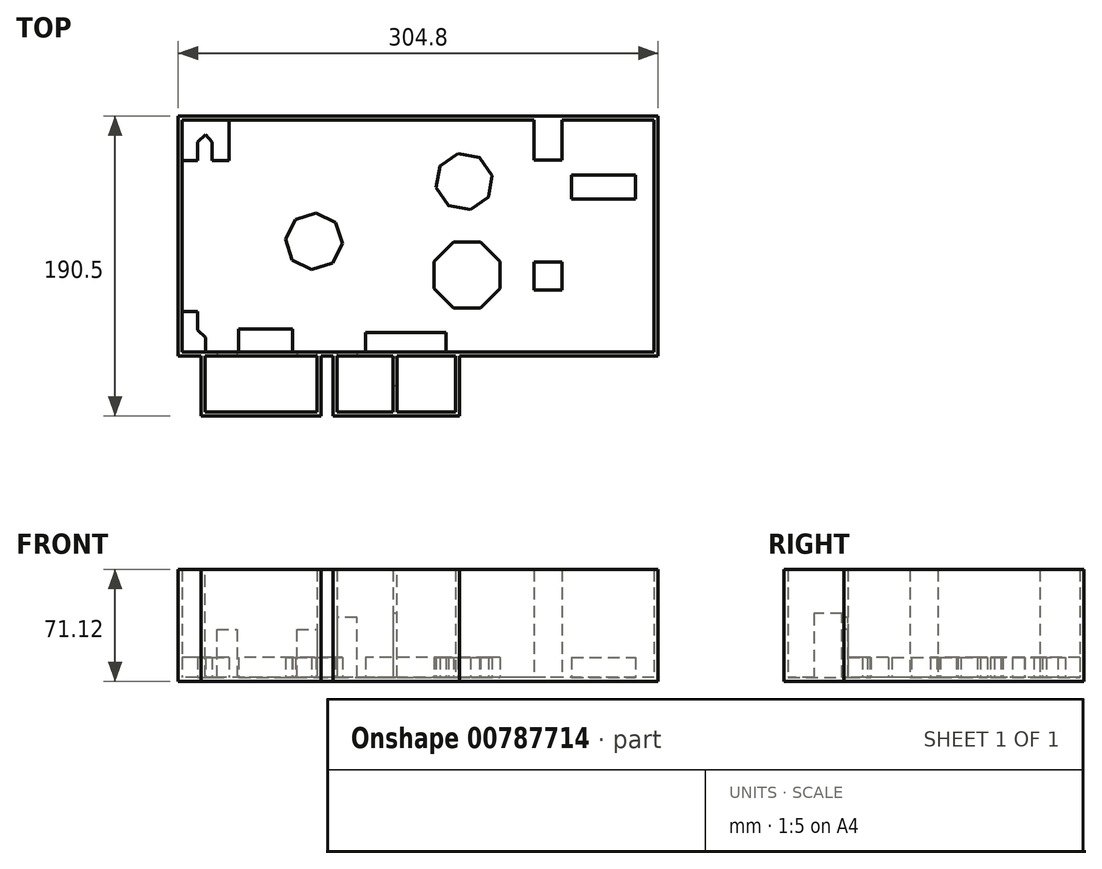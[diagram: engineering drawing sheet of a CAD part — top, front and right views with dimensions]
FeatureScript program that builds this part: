
annotation { "Feature Type Name" : "Feature", "Feature Type Description" : "" }
export const myFeature = defineFeature(function(context is Context, id is Id, definition is map)
    precondition{}
    {
        {
            var Q0;
            Q0=qCreatedBy(makeId("Top.planeOp"),FACE);
            var sketch = newSketch(context, id + "F0", { "sketchPlane" : qUnion([Q0])});
            skLineSegment(sketch, "E0.bottom", {"start": v(76.2, 76.2) * mm, "end": v(-228.6, 76.2) * mm});
            skLineSegment(sketch, "E0.top", {"start": v(76.2, -76.2) * mm, "end": v(-228.6, -76.2) * mm});
            skLineSegment(sketch, "E0.left", {"start": v(76.2, 76.2) * mm, "end": v(76.2, -76.2) * mm});
            skLineSegment(sketch, "E0.right", {"start": v(-228.6, 76.2) * mm, "end": v(-228.6, -76.2) * mm});
            skPoint(sketch, "E1", {"position": v(0, 76.2) * mm});
            skPoint(sketch, "E2", {"position": v(12.7, 76.2) * mm});
            skLineSegment(sketch, "E3", {"start": v(0, 76.2) * mm, "end": v(0, 50.8) * mm});
            skLineSegment(sketch, "E4", {"start": v(0, 50.8) * mm, "end": v(12.7, 50.8) * mm});
            skLineSegment(sketch, "E5", {"start": v(12.7, 50.8) * mm, "end": v(12.7, 76.2) * mm});
            skPoint(sketch, "E6", {"position": v(0, -31.67) * mm});
            skPoint(sketch, "E7", {"position": v(0, -18.97) * mm});
            skLineSegment(sketch, "E8", {"start": v(0, -31.67) * mm, "end": v(0, -18.97) * mm});
            skLineSegment(sketch, "E9", {"start": v(0, -18.97) * mm, "end": v(12.7, -18.97) * mm});
            skLineSegment(sketch, "E10", {"start": v(12.7, -18.97) * mm, "end": v(12.7, -31.67) * mm});
            skLineSegment(sketch, "E11", {"start": v(12.7, -31.67) * mm, "end": v(0, -31.67) * mm});
            skPoint(sketch, "E12", {"position": v(18.54, 76.2) * mm});
            skPoint(sketch, "E13", {"position": v(33.78, 76.2) * mm});
            skPoint(sketch, "E14", {"position": v(-228.6, -42.42) * mm});
            skPoint(sketch, "E15", {"position": v(-228.6, -17.02) * mm});
            skPoint(sketch, "E16", {"position": v(-201.42, -76.2) * mm});
            skPoint(sketch, "E17", {"position": v(-188.72, -76.2) * mm});
            skPoint(sketch, "E18", {"position": v(-150.62, -76.2) * mm});
            skPoint(sketch, "E19", {"position": v(-137.92, -76.2) * mm});
            skLineSegment(sketch, "E20", {"start": v(-201.42, -114.3) * mm, "end": v(-137.92, -114.3) * mm});
            skLineSegment(sketch, "E21", {"start": v(-137.92, -114.3) * mm, "end": v(-137.92, -76.2) * mm});
            skLineSegment(sketch, "E22", {"start": v(-201.42, -114.3) * mm, "end": v(-214.12, -114.3) * mm});
            skLineSegment(sketch, "E23", {"start": v(-214.12, -114.3) * mm, "end": v(-214.12, -76.2) * mm});
            skPoint(sketch, "E24", {"position": v(-130.3, -76.2) * mm});
            skLineSegment(sketch, "E25", {"start": v(-130.3, -76.2) * mm, "end": v(-130.3, -114.3) * mm});
            skLineSegment(sketch, "E26", {"start": v(-130.3, -114.3) * mm, "end": v(-92.2, -114.3) * mm});
            skLineSegment(sketch, "E27", {"start": v(-92.2, -114.3) * mm, "end": v(-49.89, -114.3) * mm});
            skLineSegment(sketch, "E28", {"start": v(-49.89, -114.3) * mm, "end": v(-49.89, -76.2) * mm});
            skLineSegment(sketch, "E29", {"start": v(-137.92, -114.3) * mm, "end": v(-130.3, -114.3) * mm});
            skPoint(sketch, "E30", {"position": v(-117.6, -76.2) * mm});
            skLineSegment(sketch, "E31", {"start": v(-92.2, -114.3) * mm, "end": v(-92.2, -76.2) * mm});
            skPoint(sketch, "E32", {"position": v(-92.2, -80) * mm});
            skPoint(sketch, "E33", {"position": v(-92.2, -92.7) * mm});
            skSolve(sketch);
        }
        {
            var Q0;
            {var subQ3=sQuery(id+"F0.wireOp",EDGE,"E0.left");Q0=makeQuery(id+"F0.imprint","IMPRINT",FACE,{"disambiguationData":[TD([[makeQuery(id+"F0.imprint","IMPRINT",EDGE,{"derivedFrom":subQ3}),-1.0]])]});}
            extrude(context, id + "F1", {"entities" : qUnion([Q0]), "depth" : 71.12 * mm, "offsetDistance" : 25.4 * mm});
        }
        {
            var Q0;
            Q0=makeQuery(id+"F1.opExtrude","CAP_FACE",FACE,{"disambiguationData":[OSD([sQuery(id+"F0.wireOp",EDGE,"E0.bottom"),sQuery(id+"F0.wireOp",EDGE,"E0.top"),sQuery(id+"F0.wireOp",EDGE,"E0.left"),sQuery(id+"F0.wireOp",EDGE,"E0.right"),sQuery(id+"F0.wireOp",EDGE,"E3"),sQuery(id+"F0.wireOp",EDGE,"E4"),sQuery(id+"F0.wireOp",EDGE,"E5"),sQuery(id+"F0.wireOp",EDGE,"E8"),sQuery(id+"F0.wireOp",EDGE,"E9"),sQuery(id+"F0.wireOp",EDGE,"E10"),sQuery(id+"F0.wireOp",EDGE,"E11")])],"isStart":false});
            shell(context, id + "F2", {"entities" : qUnion([Q0]), "thickness" : 2.54 * mm});
        }
        {
            var Q0;
            Q0=makeQuery(id+"F0.imprint","IMPRINT",FACE,{"disambiguationData":[TD([[makeQuery(id+"F0.imprint","IMPRINT",EDGE,{"derivedFrom":sQuery(id+"F0.wireOp",EDGE,"E8")}),-1.0]])]});
            extrude(context, id + "F3", {"entities" : qUnion([Q0]), "operationType" : NewBodyOperationType.ADD, "depth" : 71.12 * mm, "offsetDistance" : 25.4 * mm});
        }
        {
            var Q0;
            {var subQ0=sQuery(id+"F0.wireOp",EDGE,"E11");var subQ1=sQuery(id+"F0.wireOp",EDGE,"E10");var subQ2=sQuery(id+"F0.wireOp",EDGE,"E9");var subQ3=sQuery(id+"F0.wireOp",EDGE,"E8");var subQ4=sQuery(id+"F0.wireOp",EDGE,"E5");var subQ5=sQuery(id+"F0.wireOp",EDGE,"E4");var subQ6=sQuery(id+"F0.wireOp",EDGE,"E3");var subQ7=sQuery(id+"F0.wireOp",EDGE,"E0.right");var subQ8=sQuery(id+"F0.wireOp",EDGE,"E0.left");var subQ9=sQuery(id+"F0.wireOp",EDGE,"E0.top");var subQ10=sQuery(id+"F0.wireOp",EDGE,"E0.bottom");Q0=makeQuery(id+"F2.opShell","OFFSET_FACE",FACE,{"disambiguationData":[OSD([subQ10,subQ9,subQ8,subQ7,subQ6,subQ5,subQ4,subQ3,subQ2,subQ1,subQ0]),TDD([makeQuery(id+"F1.opExtrude","CAP_FACE",FACE,{"disambiguationData":[OSD([subQ10,subQ9,subQ8,subQ7,subQ6,subQ5,subQ4,subQ3,subQ2,subQ1,subQ0])],"isStart":true})])]});}
            var sketch = newSketch(context, id + "F4", { "sketchPlane" : qUnion([Q0])});
            skLineSegment(sketch, "E34.0.0", {"start": v(15.24, 73.66) * mm, "end": v(15.24, 48.26) * mm});
            skLineSegment(sketch, "E34.0.1", {"start": v(15.24, 48.26) * mm, "end": v(-2.54, 48.26) * mm});
            skLineSegment(sketch, "E34.0.2", {"start": v(-2.54, 48.26) * mm, "end": v(-2.54, 73.66) * mm});
            skLineSegment(sketch, "E34.0.3", {"start": v(-2.54, 73.66) * mm, "end": v(-226.06, 73.66) * mm});
            skLineSegment(sketch, "E34.0.4", {"start": v(-226.06, 73.66) * mm, "end": v(-226.06, -73.66) * mm});
            skLineSegment(sketch, "E34.0.5", {"start": v(-226.06, -73.66) * mm, "end": v(73.66, -73.66) * mm});
            skLineSegment(sketch, "E34.0.6", {"start": v(73.66, -73.66) * mm, "end": v(73.66, 73.66) * mm});
            skLineSegment(sketch, "E34.0.7", {"start": v(73.66, 73.66) * mm, "end": v(15.24, 73.66) * mm});
            skPoint(sketch, "E35", {"position": v(21.08, 73.66) * mm});
            skPoint(sketch, "E36", {"position": v(33.78, 73.66) * mm});
            skPoint(sketch, "E37", {"position": v(-198.88, -73.66) * mm});
            skPoint(sketch, "E38", {"position": v(-226.06, -39.88) * mm});
            skPoint(sketch, "E39", {"position": v(-226.06, -14.48) * mm});
            skSolve(sketch);
        }
        {
            var Q0;
            Q0=makeQuery(id+"F0.imprint","IMPRINT",FACE,{"disambiguationData":[TD([[makeQuery(id+"F0.imprint","IMPRINT",EDGE,{"derivedFrom":sQuery(id+"F0.wireOp",EDGE,"E20")}),1.0]])]});
            extrude(context, id + "F5", {"entities" : qUnion([Q0]), "operationType" : NewBodyOperationType.ADD, "depth" : 71.12 * mm, "offsetDistance" : 25.4 * mm});
        }
        {
            var Q0;
            {var subQ0=sQuery(id+"F0.wireOp",EDGE,"E0.top");var subQ1=sQuery(id+"F0.wireOp",EDGE,"E11");var subQ2=sQuery(id+"F0.wireOp",EDGE,"E10");var subQ3=sQuery(id+"F0.wireOp",EDGE,"E9");var subQ4=sQuery(id+"F0.wireOp",EDGE,"E8");var subQ5=sQuery(id+"F0.wireOp",EDGE,"E5");var subQ6=sQuery(id+"F0.wireOp",EDGE,"E4");var subQ7=sQuery(id+"F0.wireOp",EDGE,"E3");var subQ8=sQuery(id+"F0.wireOp",EDGE,"E0.right");var subQ9=sQuery(id+"F0.wireOp",EDGE,"E0.left");var subQ10=sQuery(id+"F0.wireOp",EDGE,"E0.bottom");Q0=makeQuery(id+"F5.boolean.opBoolean","MERGE",FACE,{"derivedFrom":[makeQuery(id+"F2.opShell","OFFSET_FACE",FACE,{"disambiguationData":[OSD([subQ10,subQ0,subQ9,subQ8,subQ7,subQ6,subQ5,subQ4,subQ3,subQ2,subQ1]),TDD([makeQuery(id+"F1.opExtrude","CAP_FACE",FACE,{"disambiguationData":[OSD([subQ10,subQ0,subQ9,subQ8,subQ7,subQ6,subQ5,subQ4,subQ3,subQ2,subQ1])],"isStart":false})])]}),makeQuery(id+"F5.opExtrude","CAP_FACE",FACE,{"disambiguationData":[OSD([subQ0,sQuery(id+"F0.wireOp",EDGE,"E20"),sQuery(id+"F0.wireOp",EDGE,"E21"),sQuery(id+"F0.wireOp",EDGE,"E22"),sQuery(id+"F0.wireOp",EDGE,"E23")])],"isStart":false})]});}
            shell(context, id + "F6", {"entities" : qUnion([Q0]), "thickness" : 2.54 * mm});
        }
        {
            var Q0;
            Q0=makeQuery(id+"F6.opShell","OFFSET_FACE",FACE,{"disambiguationData":[OSD([sQuery(id+"F0.wireOp",EDGE,"E0.top")])]});
            var sketch = newSketch(context, id + "F7", { "sketchPlane" : qUnion([Q0])});
            skLineSegment(sketch, "E40.0.0", {"start": v(-140.46, 2.54) * mm, "end": v(-211.58, 2.54) * mm});
            skLineSegment(sketch, "E40.0.2", {"start": v(-211.58, 2.54) * mm, "end": v(-140.46, 2.54) * mm});
            skPoint(sketch, "E41", {"position": v(-153.16, 2.54) * mm});
            skPoint(sketch, "E42", {"position": v(-191.26, 2.54) * mm});
            skPoint(sketch, "E43", {"position": v(-203.96, 2.54) * mm});
            skLineSegment(sketch, "E44", {"start": v(-203.96, 2.54) * mm, "end": v(-203.96, 33.02) * mm});
            skLineSegment(sketch, "E45", {"start": v(-203.96, 33.02) * mm, "end": v(-191.26, 33.02) * mm});
            skLineSegment(sketch, "E46", {"start": v(-191.26, 33.02) * mm, "end": v(-191.26, 2.54) * mm});
            skLineSegment(sketch, "E47", {"start": v(-153.16, 2.54) * mm, "end": v(-153.16, 33.02) * mm});
            skLineSegment(sketch, "E48", {"start": v(-153.16, 33.02) * mm, "end": v(-140.46, 33.02) * mm});
            skLineSegment(sketch, "E49", {"start": v(-140.46, 33.02) * mm, "end": v(-140.46, 2.54) * mm});
            skSolve(sketch);
        }
        {
            var Q0;
            {var subQ0=sQuery(id+"F7.wireOp",EDGE,"E44");Q0=makeQuery(id+"F7.imprint","IMPRINT",FACE,{"disambiguationData":[TD([[makeQuery(id+"F7.imprint","IMPRINT",EDGE,{"derivedFrom":subQ0}),-1.0]])]});}
            var Q1;
            {var subQ2=sQuery(id+"F7.wireOp",EDGE,"E47");Q1=makeQuery(id+"F7.imprint","IMPRINT",FACE,{"disambiguationData":[TD([[makeQuery(id+"F7.imprint","IMPRINT",EDGE,{"derivedFrom":subQ2}),-1.0]])]});}
            extrude(context, id + "F8", {"entities" : qUnion([Q0, Q1]), "operationType" : NewBodyOperationType.REMOVE, "oppositeDirection" : true, "depth" : 25.4 * mm, "offsetDistance" : 25.4 * mm});
        }
        {
            var Q0;
            Q0=makeQuery(id+"F0.imprint","IMPRINT",FACE,{"disambiguationData":[TD([[makeQuery(id+"F0.imprint","IMPRINT",EDGE,{"derivedFrom":sQuery(id+"F0.wireOp",EDGE,"E27")}),1.0]])]});
            extrude(context, id + "F9", {"entities" : qUnion([Q0]), "operationType" : NewBodyOperationType.ADD, "depth" : 71.12 * mm, "offsetDistance" : 25.4 * mm});
        }
        {
            var Q0;
            {var subQ0=sQuery(id+"F0.wireOp",EDGE,"E0.top");var subQ1=sQuery(id+"F0.wireOp",EDGE,"E11");var subQ2=sQuery(id+"F0.wireOp",EDGE,"E10");var subQ3=sQuery(id+"F0.wireOp",EDGE,"E9");var subQ4=sQuery(id+"F0.wireOp",EDGE,"E8");var subQ5=sQuery(id+"F0.wireOp",EDGE,"E5");var subQ6=sQuery(id+"F0.wireOp",EDGE,"E4");var subQ7=sQuery(id+"F0.wireOp",EDGE,"E3");var subQ8=sQuery(id+"F0.wireOp",EDGE,"E0.right");var subQ9=sQuery(id+"F0.wireOp",EDGE,"E0.left");var subQ10=sQuery(id+"F0.wireOp",EDGE,"E0.bottom");Q0=makeQuery(id+"F9.boolean.opBoolean","MERGE",FACE,{"derivedFrom":[makeQuery(id+"F5.boolean.opBoolean","MERGE",FACE,{"derivedFrom":[makeQuery(id+"F2.opShell","OFFSET_FACE",FACE,{"disambiguationData":[OSD([subQ10,subQ0,subQ9,subQ8,subQ7,subQ6,subQ5,subQ4,subQ3,subQ2,subQ1]),TDD([makeQuery(id+"F1.opExtrude","CAP_FACE",FACE,{"disambiguationData":[OSD([subQ10,subQ0,subQ9,subQ8,subQ7,subQ6,subQ5,subQ4,subQ3,subQ2,subQ1])],"isStart":false})])]}),makeQuery(id+"F5.opExtrude","CAP_FACE",FACE,{"disambiguationData":[OSD([subQ0,sQuery(id+"F0.wireOp",EDGE,"E20"),sQuery(id+"F0.wireOp",EDGE,"E21"),sQuery(id+"F0.wireOp",EDGE,"E22"),sQuery(id+"F0.wireOp",EDGE,"E23")])],"isStart":false})]}),makeQuery(id+"F9.opExtrude","CAP_FACE",FACE,{"disambiguationData":[OSD([subQ0,sQuery(id+"F0.wireOp",EDGE,"E27"),sQuery(id+"F0.wireOp",EDGE,"E28"),sQuery(id+"F0.wireOp",EDGE,"E31")])],"isStart":false})]});}
            shell(context, id + "F10", {"entities" : qUnion([Q0]), "thickness" : 2.54 * mm});
        }
        {
            var Q0;
            Q0=makeQuery(id+"F10.opShell","OFFSET_FACE",FACE,{"disambiguationData":[OSD([sQuery(id+"F0.wireOp",EDGE,"E31")])]});
            var sketch = newSketch(context, id + "F11", { "sketchPlane" : qUnion([Q0])});
            skLineSegment(sketch, "E50.0", {"start": v(-111.76, 2.54) * mm, "end": v(-76.2, 2.54) * mm});
            skLineSegment(sketch, "E51.0.0", {"start": v(-76.2, 2.54) * mm, "end": v(-76.2, 71.12) * mm});
            skLineSegment(sketch, "E51.0.1", {"start": v(-76.2, 71.12) * mm, "end": v(-111.76, 71.12) * mm});
            skLineSegment(sketch, "E51.0.2", {"start": v(-111.76, 71.12) * mm, "end": v(-111.76, 2.54) * mm});
            skPoint(sketch, "E52", {"position": v(-80, 2.54) * mm});
            skPoint(sketch, "E53", {"position": v(-92.7, 2.54) * mm});
            skLineSegment(sketch, "E54", {"start": v(-92.7, 2.54) * mm, "end": v(-92.7, 40.64) * mm});
            skLineSegment(sketch, "E55", {"start": v(-92.7, 40.64) * mm, "end": v(-80, 40.64) * mm});
            skLineSegment(sketch, "E56", {"start": v(-80, 40.64) * mm, "end": v(-80, 2.54) * mm});
            skSolve(sketch);
        }
        {
            var Q0;
            {var subQ0=sQuery(id+"F11.wireOp",EDGE,"E54");Q0=makeQuery(id+"F11.imprint","IMPRINT",FACE,{"disambiguationData":[TD([[makeQuery(id+"F11.imprint","IMPRINT",EDGE,{"derivedFrom":subQ0}),-1.0]])]});}
            extrude(context, id + "F12", {"entities" : qUnion([Q0]), "operationType" : NewBodyOperationType.REMOVE, "oppositeDirection" : true, "depth" : 25.4 * mm, "offsetDistance" : 25.4 * mm});
        }
        {
            var Q0;
            {var subQ0=sQuery(id+"F0.wireOp",EDGE,"E25");Q0=makeQuery(id+"F0.imprint","IMPRINT",FACE,{"disambiguationData":[TD([[makeQuery(id+"F0.imprint","IMPRINT",EDGE,{"derivedFrom":subQ0}),1.0]])]});}
            extrude(context, id + "F13", {"entities" : qUnion([Q0]), "operationType" : NewBodyOperationType.ADD, "depth" : 71.12 * mm, "offsetDistance" : 25.4 * mm});
        }
        {
            var Q0;
            {var subQ0=sQuery(id+"F0.wireOp",EDGE,"E31");var subQ1=sQuery(id+"F0.wireOp",EDGE,"E0.top");var subQ2=sQuery(id+"F0.wireOp",EDGE,"E11");var subQ3=sQuery(id+"F0.wireOp",EDGE,"E10");var subQ4=sQuery(id+"F0.wireOp",EDGE,"E9");var subQ5=sQuery(id+"F0.wireOp",EDGE,"E8");var subQ6=sQuery(id+"F0.wireOp",EDGE,"E5");var subQ7=sQuery(id+"F0.wireOp",EDGE,"E4");var subQ8=sQuery(id+"F0.wireOp",EDGE,"E3");var subQ9=sQuery(id+"F0.wireOp",EDGE,"E0.right");var subQ10=sQuery(id+"F0.wireOp",EDGE,"E0.left");var subQ11=sQuery(id+"F0.wireOp",EDGE,"E0.bottom");Q0=makeQuery(id+"F13.boolean.opBoolean","MERGE",FACE,{"derivedFrom":[makeQuery(id+"F9.boolean.opBoolean","MERGE",FACE,{"derivedFrom":[makeQuery(id+"F5.boolean.opBoolean","MERGE",FACE,{"derivedFrom":[makeQuery(id+"F2.opShell","OFFSET_FACE",FACE,{"disambiguationData":[OSD([subQ11,subQ1,subQ10,subQ9,subQ8,subQ7,subQ6,subQ5,subQ4,subQ3,subQ2]),TDD([makeQuery(id+"F1.opExtrude","CAP_FACE",FACE,{"disambiguationData":[OSD([subQ11,subQ1,subQ10,subQ9,subQ8,subQ7,subQ6,subQ5,subQ4,subQ3,subQ2])],"isStart":false})])]}),makeQuery(id+"F5.opExtrude","CAP_FACE",FACE,{"disambiguationData":[OSD([subQ1,sQuery(id+"F0.wireOp",EDGE,"E20"),sQuery(id+"F0.wireOp",EDGE,"E21"),sQuery(id+"F0.wireOp",EDGE,"E22"),sQuery(id+"F0.wireOp",EDGE,"E23")])],"isStart":false})]}),makeQuery(id+"F9.opExtrude","CAP_FACE",FACE,{"disambiguationData":[OSD([subQ1,sQuery(id+"F0.wireOp",EDGE,"E27"),sQuery(id+"F0.wireOp",EDGE,"E28"),subQ0])],"isStart":false})]}),makeQuery(id+"F13.opExtrude","CAP_FACE",FACE,{"disambiguationData":[OSD([subQ1,sQuery(id+"F0.wireOp",EDGE,"E25"),sQuery(id+"F0.wireOp",EDGE,"E26"),subQ0])],"isStart":false})]});}
            shell(context, id + "F14", {"entities" : qUnion([Q0]), "thickness" : 2.54 * mm});
        }
        {
            var Q0;
            {var subQ0=sQuery(id+"F0.wireOp",EDGE,"E31");Q0=makeQuery(id+"F14.opShell","OFFSET_FACE",FACE,{"disambiguationData":[OSD([subQ0]),TDD([makeQuery(id+"F13.opExtrude","SWEPT_FACE",FACE,{"disambiguationData":[OSD([subQ0])]})])]});}
            var sketch = newSketch(context, id + "F15", { "sketchPlane" : qUnion([Q0])});
            skLineSegment(sketch, "E57.0.0", {"start": v(77.47, 2.54) * mm, "end": v(95.25, 2.54) * mm});
            skLineSegment(sketch, "E57.0.1", {"start": v(95.25, 2.54) * mm, "end": v(95.25, 43.18) * mm});
            skLineSegment(sketch, "E57.0.2", {"start": v(95.25, 43.18) * mm, "end": v(77.47, 43.18) * mm});
            skLineSegment(sketch, "E57.0.3", {"start": v(77.47, 43.18) * mm, "end": v(77.47, 2.54) * mm});
            skSolve(sketch);
        }
        {
            var Q0;
            Q0 = qSketchRegion(id + "F15", true);
            extrude(context, id + "F16", {"entities" : qUnion([Q0]), "operationType" : NewBodyOperationType.REMOVE, "oppositeDirection" : true, "depth" : 25.4 * mm, "offsetDistance" : 25.4 * mm});
        }
        {
            var Q0;
            Q0=makeQuery(id+"F14.opShell","OFFSET_FACE",FACE,{"disambiguationData":[OSD([sQuery(id+"F0.wireOp",EDGE,"E0.top")])]});
            var sketch = newSketch(context, id + "F17", { "sketchPlane" : qUnion([Q0])});
            skLineSegment(sketch, "E58.0.0", {"start": v(-92.2, 2.54) * mm, "end": v(-92.2, 71.12) * mm});
            skLineSegment(sketch, "E58.0.1", {"start": v(-92.2, 71.12) * mm, "end": v(-127.76, 71.12) * mm});
            skLineSegment(sketch, "E58.0.2", {"start": v(-127.76, 71.12) * mm, "end": v(-127.76, 2.54) * mm});
            skLineSegment(sketch, "E58.0.3", {"start": v(-127.76, 2.54) * mm, "end": v(-92.2, 2.54) * mm});
            skPoint(sketch, "E59", {"position": v(-115.06, 2.54) * mm});
            skLineSegment(sketch, "E60", {"start": v(-115.06, 2.54) * mm, "end": v(-115.06, 40.64) * mm});
            skLineSegment(sketch, "E61", {"start": v(-115.06, 40.64) * mm, "end": v(-127.76, 40.64) * mm});
            skLineSegment(sketch, "E62", {"start": v(-127.76, 40.64) * mm, "end": v(-127.76, 2.54) * mm});
            skSolve(sketch);
        }
        {
            var Q0;
            {var subQ2=sQuery(id+"F17.wireOp",EDGE,"E60");Q0=makeQuery(id+"F17.imprint","IMPRINT",FACE,{"disambiguationData":[TD([[makeQuery(id+"F17.imprint","IMPRINT",EDGE,{"derivedFrom":subQ2}),1.0]])]});}
            extrude(context, id + "F18", {"entities" : qUnion([Q0]), "operationType" : NewBodyOperationType.REMOVE, "oppositeDirection" : true, "depth" : 25.4 * mm, "offsetDistance" : 25.4 * mm});
        }
        {
            var Q0;
            Q0=makeQuery(id+"F4.imprint","IMPRINT",FACE,{"disambiguationData":[TD([[makeQuery(id+"F4.imprint","IMPRINT",EDGE,{"derivedFrom":sQuery(id+"F4.wireOp",EDGE,"E34.0.0")}),-1.0]])]});
            var sketch = newSketch(context, id + "F19", { "sketchPlane" : qUnion([Q0])});
            skLineSegment(sketch, "E63.0.0", {"start": v(15.24, 73.66) * mm, "end": v(15.24, 48.26) * mm});
            skLineSegment(sketch, "E63.0.1", {"start": v(15.24, 48.26) * mm, "end": v(-2.54, 48.26) * mm});
            skLineSegment(sketch, "E63.0.2", {"start": v(-2.54, 48.26) * mm, "end": v(-2.54, 73.66) * mm});
            skLineSegment(sketch, "E63.0.3", {"start": v(-2.54, 73.66) * mm, "end": v(-226.06, 73.66) * mm});
            skLineSegment(sketch, "E63.0.4", {"start": v(-226.06, 73.66) * mm, "end": v(-226.06, -73.66) * mm});
            skLineSegment(sketch, "E63.0.5", {"start": v(-226.06, -73.66) * mm, "end": v(73.66, -73.66) * mm});
            skLineSegment(sketch, "E63.0.6", {"start": v(73.66, -73.66) * mm, "end": v(73.66, 73.66) * mm});
            skLineSegment(sketch, "E63.0.7", {"start": v(73.66, 73.66) * mm, "end": v(15.24, 73.66) * mm});
            skLineSegment(sketch, "E64", {"start": v(-226.06, -48.08) * mm, "end": v(-216.38, -48.08) * mm});
            skLineSegment(sketch, "E65", {"start": v(-216.38, -48.08) * mm, "end": v(-216.38, -59.7) * mm});
            skLineSegment(sketch, "E66", {"start": v(-216.38, -59.7) * mm, "end": v(-211.17, -64.43) * mm});
            skLineSegment(sketch, "E67", {"start": v(-211.17, -64.43) * mm, "end": v(-211.17, -73.66) * mm});
            skPoint(sketch, "E68", {"position": v(-216.38, 48.08) * mm});
            skLineSegment(sketch, "E69", {"start": v(-216.38, 48.08) * mm, "end": v(-226.06, 48.08) * mm});
            skLineSegment(sketch, "E70", {"start": v(-216.38, 48.08) * mm, "end": v(-216.38, 59.7) * mm});
            skLineSegment(sketch, "E71", {"start": v(-216.38, 59.7) * mm, "end": v(-211.08, 64.33) * mm});
            skLineSegment(sketch, "E72", {"start": v(-211.08, 64.33) * mm, "end": v(-211.08, 73.66) * mm});
            skLineSegment(sketch, "E73", {"start": v(-211.08, 64.33) * mm, "end": v(-207.02, 59.7) * mm});
            skLineSegment(sketch, "E74", {"start": v(-207.02, 59.7) * mm, "end": v(-207.02, 48.08) * mm});
            skLineSegment(sketch, "E75", {"start": v(-207.02, 48.08) * mm, "end": v(-196.24, 48.08) * mm});
            skLineSegment(sketch, "E76", {"start": v(-196.24, 48.08) * mm, "end": v(-196.24, 73.66) * mm});
            skCircle(sketch, "E77.cCircle", {"center": v(-142.4, -3.34) * mm, "radius": 16.76 * mm, "construction": true});
            skLineSegment(sketch, "E77.0", {"start": v(-154.2, 10.46) * mm, "end": v(-140.98, 14.75) * mm});
            skLineSegment(sketch, "E77.1", {"start": v(-140.98, 14.75) * mm, "end": v(-128.61, 8.45) * mm});
            skLineSegment(sketch, "E77.2", {"start": v(-128.61, 8.45) * mm, "end": v(-124.32, -4.76) * mm});
            skLineSegment(sketch, "E77.3", {"start": v(-124.32, -4.76) * mm, "end": v(-130.62, -17.14) * mm});
            skLineSegment(sketch, "E77.4", {"start": v(-130.62, -17.14) * mm, "end": v(-143.83, -21.43) * mm});
            skLineSegment(sketch, "E77.5", {"start": v(-143.83, -21.43) * mm, "end": v(-156.2, -15.12) * mm});
            skLineSegment(sketch, "E77.6", {"start": v(-156.2, -15.12) * mm, "end": v(-160.5, -1.92) * mm});
            skLineSegment(sketch, "E77.7", {"start": v(-160.5, -1.92) * mm, "end": v(-154.2, 10.46) * mm});
            skPoint(sketch, "E77.0.midPoint", {"position": v(-147.59, 12.6) * mm});
            skCircle(sketch, "E78.cCircle", {"center": v(-46.95, 34.53) * mm, "radius": 16.8 * mm, "construction": true});
            skLineSegment(sketch, "E78.0", {"start": v(-50.8, 52.3) * mm, "end": v(-37.1, 49.83) * mm});
            skLineSegment(sketch, "E78.1", {"start": v(-37.1, 49.83) * mm, "end": v(-29.17, 38.39) * mm});
            skLineSegment(sketch, "E78.2", {"start": v(-29.17, 38.39) * mm, "end": v(-31.64, 24.68) * mm});
            skLineSegment(sketch, "E78.3", {"start": v(-31.64, 24.68) * mm, "end": v(-43.09, 16.75) * mm});
            skLineSegment(sketch, "E78.4", {"start": v(-43.09, 16.75) * mm, "end": v(-56.79, 19.22) * mm});
            skLineSegment(sketch, "E78.5", {"start": v(-56.79, 19.22) * mm, "end": v(-64.73, 30.66) * mm});
            skLineSegment(sketch, "E78.6", {"start": v(-64.73, 30.66) * mm, "end": v(-62.25, 44.37) * mm});
            skLineSegment(sketch, "E78.7", {"start": v(-62.25, 44.37) * mm, "end": v(-50.8, 52.3) * mm});
            skPoint(sketch, "E78.0.midPoint", {"position": v(-43.96, 51.07) * mm});
            skLineSegment(sketch, "E79", {"start": v(-190.26, -73.66) * mm, "end": v(-190.26, -59) * mm});
            skLineSegment(sketch, "E80", {"start": v(-190.26, -59) * mm, "end": v(-156, -59) * mm});
            skLineSegment(sketch, "E81", {"start": v(-156, -59) * mm, "end": v(-156, -73.66) * mm});
            skLineSegment(sketch, "E82", {"start": v(-109.68, -73.66) * mm, "end": v(-109.68, -61.34) * mm});
            skLineSegment(sketch, "E83", {"start": v(-109.68, -61.34) * mm, "end": v(-58.6, -61.34) * mm});
            skLineSegment(sketch, "E84", {"start": v(-58.6, -61.34) * mm, "end": v(-58.6, -73.66) * mm});
            skCircle(sketch, "E85.cCircle", {"center": v(-45.18, -24.76) * mm, "radius": 20.89 * mm, "construction": true});
            skLineSegment(sketch, "E85.0", {"start": v(-53.84, -3.88) * mm, "end": v(-36.53, -3.88) * mm});
            skLineSegment(sketch, "E85.1", {"start": v(-36.53, -3.88) * mm, "end": v(-24.3, -16.11) * mm});
            skLineSegment(sketch, "E85.2", {"start": v(-24.3, -16.11) * mm, "end": v(-24.3, -33.42) * mm});
            skLineSegment(sketch, "E85.3", {"start": v(-24.3, -33.42) * mm, "end": v(-36.53, -45.65) * mm});
            skLineSegment(sketch, "E85.4", {"start": v(-36.53, -45.65) * mm, "end": v(-53.84, -45.65) * mm});
            skLineSegment(sketch, "E85.5", {"start": v(-53.84, -45.65) * mm, "end": v(-66.07, -33.42) * mm});
            skLineSegment(sketch, "E85.6", {"start": v(-66.07, -33.42) * mm, "end": v(-66.07, -16.11) * mm});
            skLineSegment(sketch, "E85.7", {"start": v(-66.07, -16.11) * mm, "end": v(-53.84, -3.88) * mm});
            skPoint(sketch, "E85.0.midPoint", {"position": v(-45.18, -3.88) * mm});
            skLineSegment(sketch, "E86.bottom", {"start": v(21.24, 38.73) * mm, "end": v(61.88, 38.73) * mm});
            skLineSegment(sketch, "E86.top", {"start": v(21.24, 23.5) * mm, "end": v(61.88, 23.5) * mm});
            skLineSegment(sketch, "E86.left", {"start": v(21.24, 38.73) * mm, "end": v(21.24, 23.5) * mm});
            skLineSegment(sketch, "E86.right", {"start": v(61.88, 38.73) * mm, "end": v(61.88, 23.5) * mm});
            skSolve(sketch);
        }
        {
            var Q0;
            Q0=makeQuery(id+"F19.imprint","IMPRINT",FACE,{"disambiguationData":[TD([[makeQuery(id+"F19.imprint","IMPRINT",EDGE,{"derivedFrom":sQuery(id+"F19.wireOp",EDGE,"E78.0")}),-1.0]])]});
            var Q1;
            Q1=makeQuery(id+"F19.imprint","IMPRINT",FACE,{"disambiguationData":[TD([[makeQuery(id+"F19.imprint","IMPRINT",EDGE,{"derivedFrom":sQuery(id+"F19.wireOp",EDGE,"E77.0")}),-1.0]])]});
            var Q2;
            Q2=makeQuery(id+"F19.imprint","IMPRINT",FACE,{"disambiguationData":[TD([[makeQuery(id+"F19.imprint","IMPRINT",EDGE,{"derivedFrom":sQuery(id+"F19.wireOp",EDGE,"E85.0")}),-1.0]])]});
            var Q3;
            {var subQ0=sQuery(id+"F19.wireOp",EDGE,"E79");Q3=makeQuery(id+"F19.imprint","IMPRINT",FACE,{"disambiguationData":[TD([[makeQuery(id+"F19.imprint","IMPRINT",EDGE,{"derivedFrom":subQ0}),-1.0]])]});}
            var Q4;
            {var subQ0=sQuery(id+"F19.wireOp",EDGE,"E64");Q4=makeQuery(id+"F19.imprint","IMPRINT",FACE,{"disambiguationData":[TD([[makeQuery(id+"F19.imprint","IMPRINT",EDGE,{"derivedFrom":subQ0}),-1.0]])]});}
            var Q5;
            {var subQ0=sQuery(id+"F19.wireOp",EDGE,"E82");Q5=makeQuery(id+"F19.imprint","IMPRINT",FACE,{"disambiguationData":[TD([[makeQuery(id+"F19.imprint","IMPRINT",EDGE,{"derivedFrom":subQ0}),-1.0]])]});}
            var Q6;
            Q6=makeQuery(id+"F19.imprint","IMPRINT",FACE,{"disambiguationData":[TD([[makeQuery(id+"F19.imprint","IMPRINT",EDGE,{"derivedFrom":sQuery(id+"F19.wireOp",EDGE,"E86.bottom")}),-1.0]])]});
            var Q7;
            {var subQ0=sQuery(id+"F19.wireOp",EDGE,"E72");Q7=makeQuery(id+"F19.imprint","IMPRINT",FACE,{"disambiguationData":[TD([[makeQuery(id+"F19.imprint","IMPRINT",EDGE,{"derivedFrom":subQ0}),-1.0]])]});}
            var Q8;
            {var subQ0=sQuery(id+"F19.wireOp",EDGE,"E69");Q8=makeQuery(id+"F19.imprint","IMPRINT",FACE,{"disambiguationData":[TD([[makeQuery(id+"F19.imprint","IMPRINT",EDGE,{"derivedFrom":subQ0}),-1.0]])]});}
            extrude(context, id + "F20", {"entities" : qUnion([Q0, Q1, Q2, Q3, Q4, Q5, Q6, Q7, Q8]), "operationType" : NewBodyOperationType.ADD, "depth" : 12.7 * mm, "offsetDistance" : 25.4 * mm});
        }
        {
            var Q0;
            {var subQ0=sQuery(id+"F0.wireOp",EDGE,"E3");Q0=makeQuery(id+"F0.imprint","IMPRINT",FACE,{"disambiguationData":[TD([[makeQuery(id+"F0.imprint","IMPRINT",EDGE,{"derivedFrom":subQ0}),1.0]])]});}
            extrude(context, id + "F21", {"entities" : qUnion([Q0]), "operationType" : NewBodyOperationType.ADD, "depth" : 71.12 * mm, "offsetDistance" : 25.4 * mm});
        }
    });
